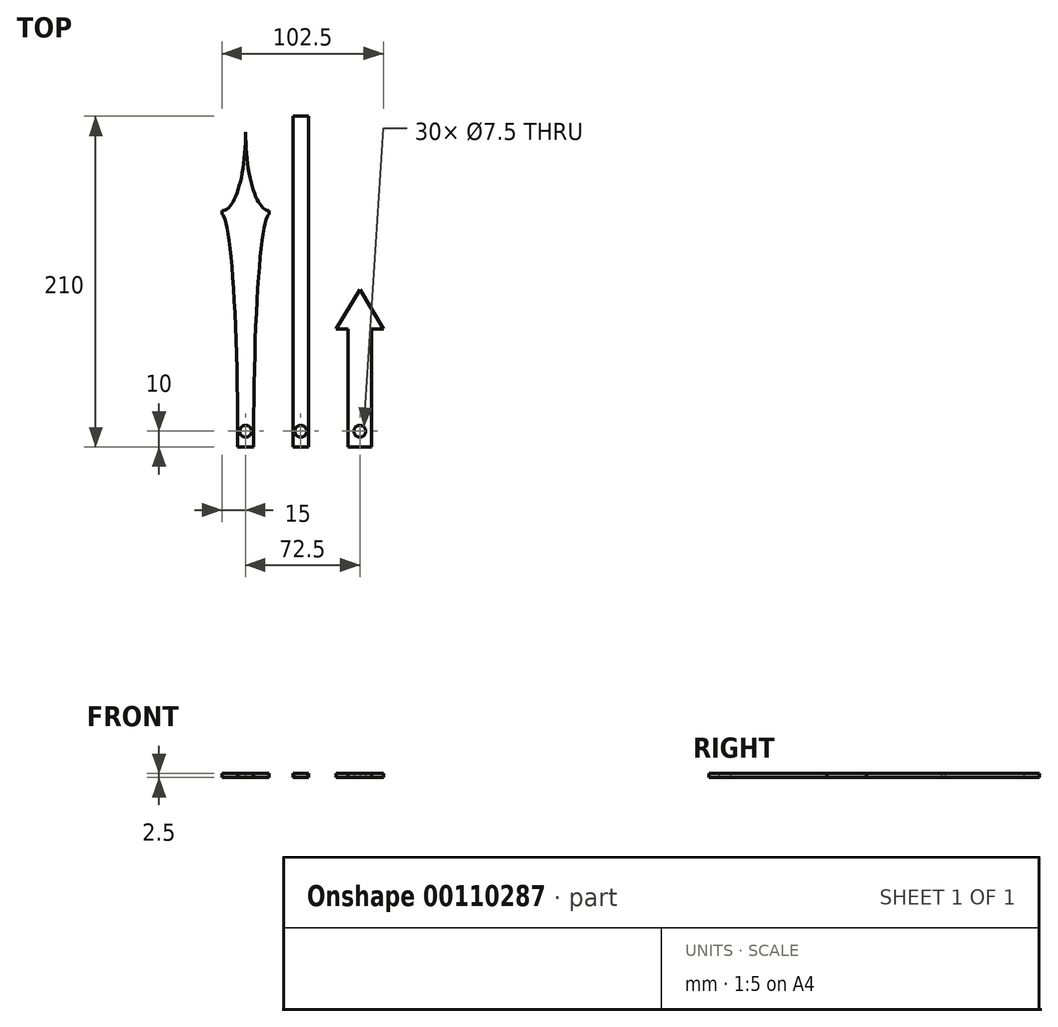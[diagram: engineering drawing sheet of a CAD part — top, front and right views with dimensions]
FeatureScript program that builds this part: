
annotation { "Feature Type Name" : "Feature", "Feature Type Description" : "" }
export const myFeature = defineFeature(function(context is Context, id is Id, definition is map)
    precondition{}
    {
        {
            var Q0;
            Q0=qCreatedBy(makeId("Top.planeOp"),FACE);
            var sketch = newSketch(context, id + "F0", { "sketchPlane" : qUnion([Q0])});
            skLineSegment(sketch, "E0", {"start": v(0, 0) * mm, "end": v(0, 150) * mm});
            skLineSegment(sketch, "E1", {"start": v(0, 150) * mm, "end": v(15, 150) * mm});
            skLineSegment(sketch, "E2", {"start": v(0, 150) * mm, "end": v(0, 200) * mm});
            skLineSegment(sketch, "E3", {"start": v(0, 0) * mm, "end": v(5, 0) * mm});
            skLineSegment(sketch, "E4", {"start": v(5, 0) * mm, "end": v(5, 75) * mm});
            skLineSegment(sketch, "E5.0", {"start": v(5, 147.5) * mm, "end": v(15, 147.5) * mm});
            skEllipticalArc(sketch, "E6", {});
            skLineSegment(sketch, "E7", {"start": v(15, 147.5) * mm, "end": v(15, 150) * mm});
            skEllipticalArc(sketch, "E8", {});
            skPoint(sketch, "E9.orphan", {"position": v(5, 200) * mm});
            skPoint(sketch, "E10.orphan", {"position": v(0, 147.5) * mm});
            skLineSegment(sketch, "E11.trimOffspring", {"start": v(5, 147.5) * mm, "end": v(5, 150) * mm});
            skEllipticalArc(sketch, "E12.MirrorCS", {});
            skEllipticalArc(sketch, "E13.MirrorCS", {});
            skLineSegment(sketch, "E14.MirrorCS", {"start": v(-15, 147.5) * mm, "end": v(-15, 150) * mm});
            skLineSegment(sketch, "E15.MirrorCS", {"start": v(0, 0) * mm, "end": v(-5, 0) * mm});
            skCircle(sketch, "E16", {"center": v(0, 10) * mm, "radius": 3.75 * mm});
            const initialGuessF0  = {"E6": [0.015, 0, 0, -1, 0.1475, 0.01, 3.141592653589793, 4.71238898038469], "E8": [0.015, 0.2, -1, 0, 0.015, 0.05, 6.283185307179586, 1.5707963267948966], "E12.MirrorCS": [-0.015, 0.2, 1, 0, 0.015, 0.05, 4.71238898038469, 6.283185307179586], "E13.MirrorCS": [-0.015, 0, 0, -1, 0.1475, 0.01, 1.5707963267948966, 3.141592653589793]};
            skSetInitialGuess(sketch, initialGuessF0);
            skSolve(sketch);
        }
        {
            var Q0;
            {var subQ0=sQuery(id+"F0.wireOp",EDGE,"E3");Q0=makeQuery(id+"F0.imprint","IMPRINT",FACE,{"disambiguationData":[TD([[makeQuery(id+"F0.imprint","IMPRINT",EDGE,{"derivedFrom":subQ0}),1.0]])]});}
            var Q1;
            Q1=makeQuery(id+"F0.imprint","IMPRINT",FACE,{"disambiguationData":[TD([[makeQuery(id+"F0.imprint","IMPRINT",EDGE,{"derivedFrom":sQuery(id+"F0.wireOp",EDGE,"E5.0")}),1.0]])]});
            var Q2;
            {var subQ0=sQuery(id+"F0.wireOp",EDGE,"E2");Q2=makeQuery(id+"F0.imprint","IMPRINT",FACE,{"disambiguationData":[TD([[makeQuery(id+"F0.imprint","IMPRINT",EDGE,{"derivedFrom":subQ0}),-1.0]])]});}
            var Q3;
            {var subQ0=sQuery(id+"F0.wireOp",EDGE,"E2");Q3=makeQuery(id+"F0.imprint","IMPRINT",FACE,{"disambiguationData":[TD([[makeQuery(id+"F0.imprint","IMPRINT",EDGE,{"derivedFrom":subQ0}),1.0]])]});}
            extrude(context, id + "F1", {"entities" : qUnion([Q0, Q1, Q2, Q3]), "depth" : 2.5 * mm});
        }
        {
            var Q0;
            Q0=qCreatedBy(makeId("Top.planeOp"),FACE);
            var sketch = newSketch(context, id + "F2", { "sketchPlane" : qUnion([Q0])});
            skLineSegment(sketch, "E17", {"start": v(30, 0) * mm, "end": v(40, 0) * mm});
            skLineSegment(sketch, "E18", {"start": v(40, 0) * mm, "end": v(40, 210) * mm});
            skLineSegment(sketch, "E19", {"start": v(30, 0) * mm, "end": v(30, 210) * mm});
            skLineSegment(sketch, "E20", {"start": v(30, 210) * mm, "end": v(40, 210) * mm});
            skLineSegment(sketch, "E21", {"start": v(0, 0) * mm, "end": v(30, 0) * mm});
            skCircle(sketch, "E22", {"center": v(35, 10) * mm, "radius": 3.75 * mm});
            skLineSegment(sketch, "E23", {"start": v(35, 0) * mm, "end": v(35, 10) * mm, "construction": true});
            skSolve(sketch);
        }
        {
            var Q0;
            Q0=qSketchRegion(id+"F2",true);
            extrude(context, id + "F3", {"entities" : qUnion([Q0]), "depth" : 2.5 * mm});
        }
        {
            var Q0;
            Q0=qCreatedBy(makeId("Top.planeOp"),FACE);
            var sketch = newSketch(context, id + "F4", { "sketchPlane" : qUnion([Q0])});
            skLineSegment(sketch, "E24", {"start": v(65, 0) * mm, "end": v(80, 0) * mm});
            skLineSegment(sketch, "E25", {"start": v(65, 0) * mm, "end": v(65, 75) * mm});
            skLineSegment(sketch, "E26", {"start": v(65, 75) * mm, "end": v(57.5, 75) * mm});
            skLineSegment(sketch, "E27", {"start": v(57.5, 75) * mm, "end": v(72.5, 100) * mm});
            skLineSegment(sketch, "E28", {"start": v(72.5, 100) * mm, "end": v(72.5, 0) * mm, "construction": true});
            skPoint(sketch, "E28.endSnap0", {"position": v(72.5, 0) * mm});
            skLineSegment(sketch, "E29", {"start": v(0, 0) * mm, "end": v(65, 0) * mm});
            skLineSegment(sketch, "E30.MirrorCS", {"start": v(80, 0) * mm, "end": v(80, 75) * mm});
            skLineSegment(sketch, "E31.MirrorCS", {"start": v(87.5, 75) * mm, "end": v(72.5, 100) * mm});
            skLineSegment(sketch, "E32.MirrorCS", {"start": v(80, 75) * mm, "end": v(87.5, 75) * mm});
            skCircle(sketch, "E33", {"center": v(72.5, 10) * mm, "radius": 3.75 * mm});
            skSolve(sketch);
        }
        {
            var Q0;
            Q0=qSketchRegion(id+"F4",true);
            extrude(context, id + "F5", {"entities" : qUnion([Q0]), "depth" : 2.5 * mm});
        }
    });
